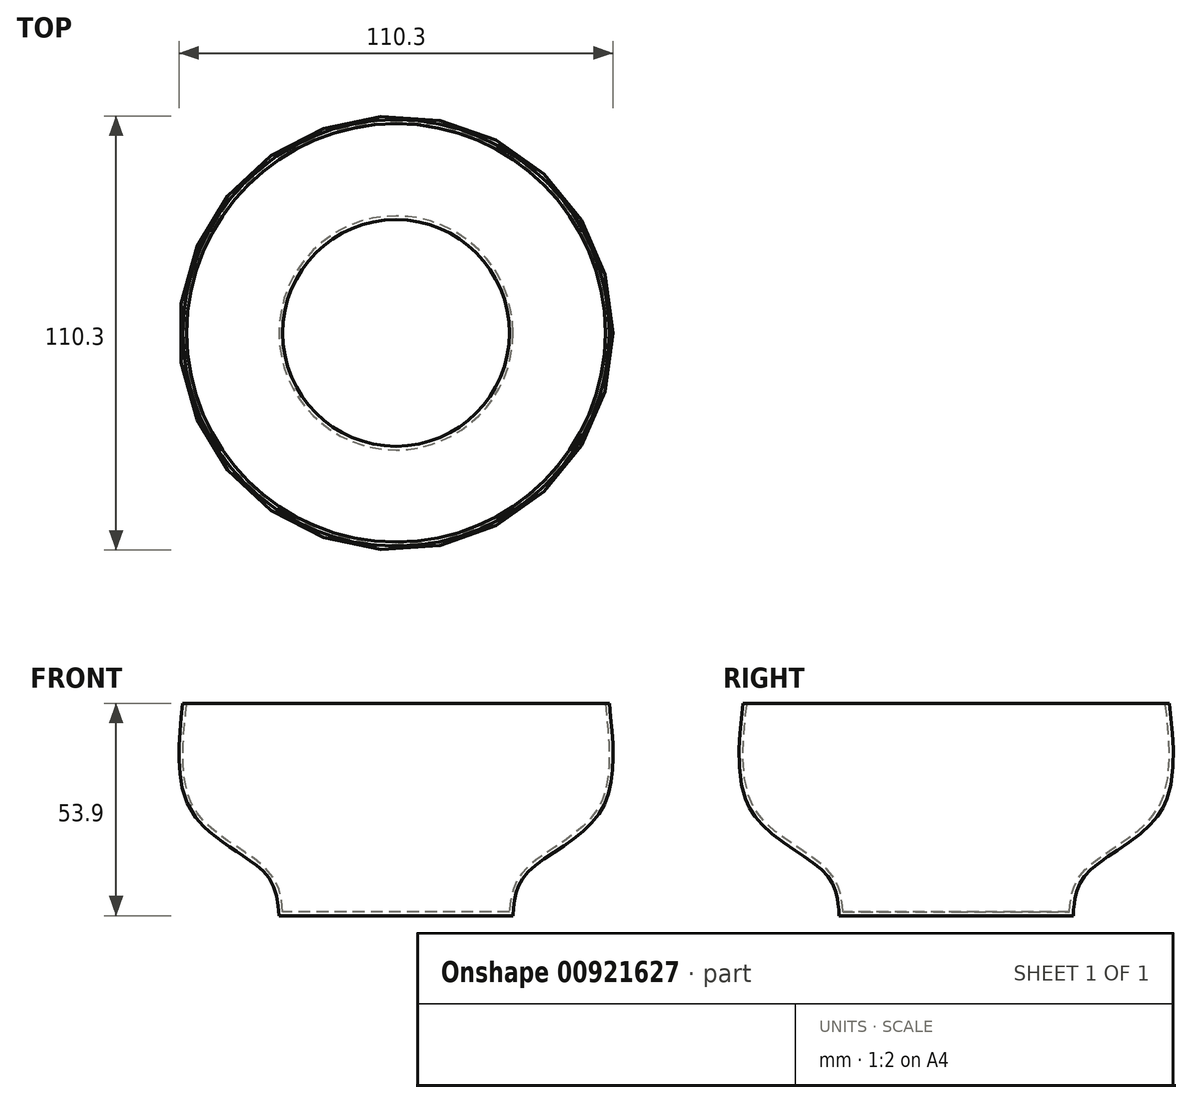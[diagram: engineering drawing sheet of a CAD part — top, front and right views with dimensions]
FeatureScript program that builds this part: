
annotation { "Feature Type Name" : "Feature", "Feature Type Description" : "" }
export const myFeature = defineFeature(function(context is Context, id is Id, definition is map)
    precondition{}
    {
        {
            var Q0;
            Q0=qCreatedBy(makeId("Front.planeOp"),FACE);
            var sketch = newSketch(context, id + "F0", { "sketchPlane" : qUnion([Q0])});
            skFitSpline(sketch, "E0", {"points": [v(-54.17, 53.9) * mm, v(-51.46, 25.66) * mm, v(-33, 10.45) * mm, v(-29.73, 0) * mm], "startDerivative": vector(-8.66, -80.1) * mm, "endDerivative": vector(2.82, -44.42) * mm});
            skLineSegment(sketch, "E1", {"start": v(-54.17, 53.9) * mm, "end": v(0, 53.9) * mm});
            skLineSegment(sketch, "E2", {"start": v(0, 53.9) * mm, "end": v(0, 0) * mm});
            skLineSegment(sketch, "E3", {"start": v(0, 0) * mm, "end": v(-29.73, 0) * mm});
            skSolve(sketch);
        }
        {
            var Q0;
            Q0=makeQuery(id+"F0.imprint","IMPRINT",FACE,{"disambiguationData":[TD([[makeQuery(id+"F0.imprint","IMPRINT",EDGE,{"derivedFrom":sQuery(id+"F0.wireOp",EDGE,"E0")}),1.0]])]});
            var Q1;
            Q1=sQuery(id+"F0.wireOp",EDGE,"E2");
            revolve(context, id + "F1", {"surfaceOperationType" : NewSurfaceOperationType.NEW, "entities" : qUnion([Q0]), "axis" : qUnion([Q1]), "revolveType" : RevolveType.FULL});
        }
        {
            var Q0;
            Q0=makeQuery(id+"F1.opRevolve","SWEPT_FACE",FACE,{"disambiguationData":[OSD([sQuery(id+"F0.wireOp",EDGE,"E1")])]});
            shell(context, id + "F2", {"entities" : qUnion([Q0]), "thickness" : 1 * mm});
        }
    });
